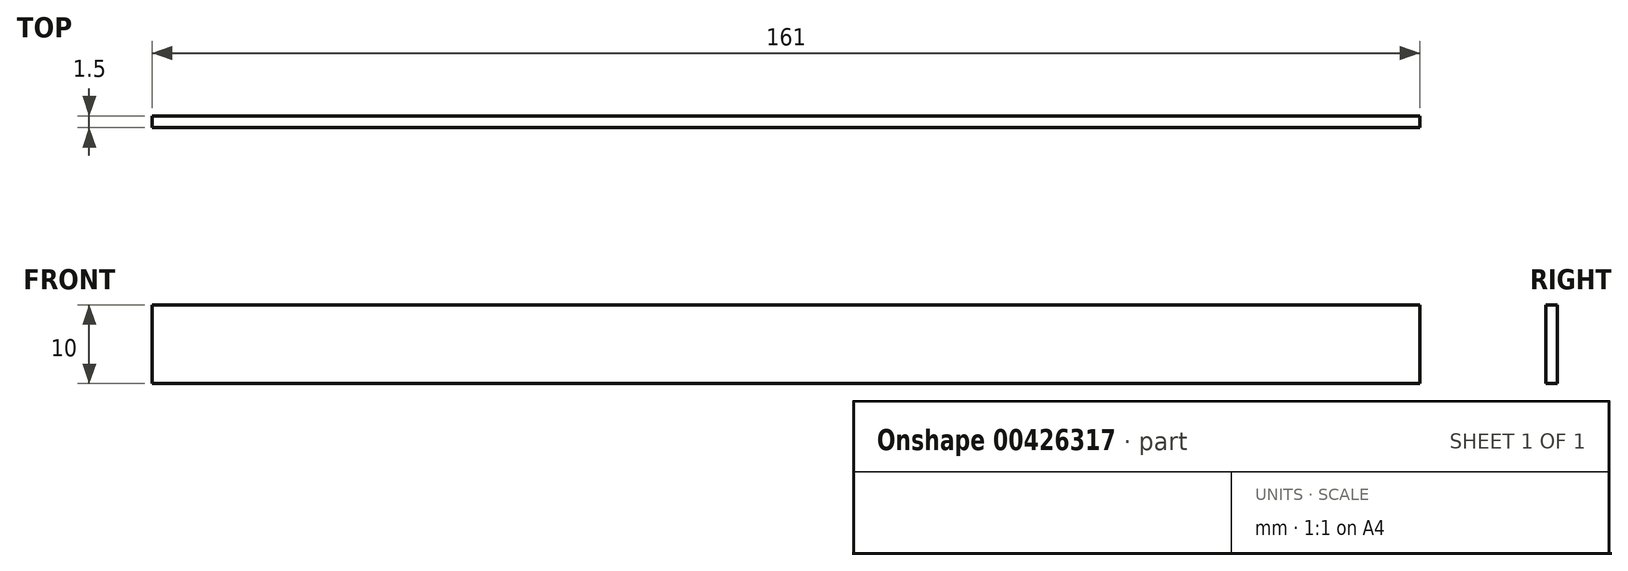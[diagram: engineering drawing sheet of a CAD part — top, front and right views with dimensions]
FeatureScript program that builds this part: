
annotation { "Feature Type Name" : "Feature", "Feature Type Description" : "" }
export const myFeature = defineFeature(function(context is Context, id is Id, definition is map)
    precondition{}
    {
        {
            var Q0;
            Q0=qCreatedBy(makeId("Front.planeOp"),FACE);
            var sketch = newSketch(context, id + "F0", { "sketchPlane" : qUnion([Q0])});
            skLineSegment(sketch, "E0.bottom", {"start": v(80.5, 5) * mm, "end": v(-80.5, 5) * mm});
            skLineSegment(sketch, "E0.top", {"start": v(80.5, -5) * mm, "end": v(-80.5, -5) * mm});
            skLineSegment(sketch, "E0.left", {"start": v(80.5, 5) * mm, "end": v(80.5, -5) * mm});
            skLineSegment(sketch, "E0.right", {"start": v(-80.5, 5) * mm, "end": v(-80.5, -5) * mm});
            skPoint(sketch, "E0.middle", {"position": v(0, 0) * mm});
            skSolve(sketch);
        }
        {
            var Q0;
            Q0=qSketchRegion(id+"F0",true);
            extrude(context, id + "F1", {"entities" : qUnion([Q0]), "depth" : 1.5 * mm, "offsetDistance" : 25 * mm});
        }
    });
